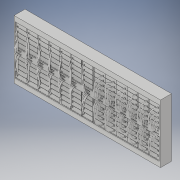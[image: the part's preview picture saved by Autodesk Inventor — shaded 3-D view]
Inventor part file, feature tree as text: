
AUTODESK INVENTOR PART (.ipt)
format: ipt  version: 2017 (Build 210142000, 142)  size: 6,932,992 bytes
history: native  units: in
note: dims shown in document units (in); Inventor stores cm internally (conversion verified against a paired STEP export)
features: sweep x35, sketch x5, extrude x3, mirror x2, plane x2, other x1
ambient origin geometry x8: Origin, YZ Plane, XZ Plane, XY Plane, X Axis, Y Axis, Z Axis, Center Point
bodies: Solid1 (feature_tree)
feature tree (48):
  extrude  "shelfing for towers"  Depth=20.0in
  other  "front of towers workplane"
  extrude  "front of towers"  Depth=0.0833in
  extrude  "towers defined"  Depth=0.5833in
  sketch  "Sketch4"  dims[d7=1.5in d8=2.9167in d9=1.5in d10=0.5833in d11=0.5833in d12=0.0833in d13=0.0833in d35=0.0833in d36=1.5in d37=2.9167in d38=1.5in d39=0.0in d40=-0.1in d47=1.5in d48=0.0in d60=0.5833in d61=0.01in d62=0.5833in d63=0.01in d64=0.5833in d65=0.01in d66=0.5833in d67=0.01in d68=0.01in d69=0.01in d70=0.01in d71=0.01in d72=0.005in d73=0.005in d74=0.005in d75=0.005in d79=0.005in d80=0.005in d81=0.005in d82=0.005in d83=0.005in d84=0.005in d85=0.005in d86=0.005in d88=0.01in d89=0.0in d90=1.5in d91=0.005in d92=0.01in d93=1.5in d94=0.01in d95=1.5in d96=0.01in d97=0.01in d98=1.5in d99=0.01in d100=1.5in d101=0.01in d102=0.01in d103=0.01in d104=0.01in d105=0.01in d106=0.01in d107=0.01in d108=0.01in d109=0.01in d110=0.01in d111=0.005in d112=0.2289in d115=0.125in d116=0.15in d117=0.15in d118=0.15in d119=0.15in d120=0.15in d121=0.125in d122=0.15in d123=0.15in d124=0.15in d125=0.15in d126=1.5in d127=0.125in d128=0.15in d129=0.15in d130=0.15in d131=0.15in d132=1.5in d133=0.125in d134=0.15in d135=0.15in d136=0.15in d137=0.15in d138=1.5in d139=0.125in d140=0.15in d141=0.15in d142=0.15in d143=0.15in d144=1.5in d145=0.125in d146=0.15in d147=0.15in d148=0.15in d149=0.15in d150=1.5in d187=0.125in d188=0.15in d189=0.15in d190=0.15in d191=0.15in d192=1.5in d193=0.2292in d194=0.15in d195=0.15in d196=0.15in d197=0.15in d198=0.15in d273=0.15in d274=0.15in d275=0.15in d276=0.15in d277=0.15in d286=1.5in d287=1.5in d288=1.5in d289=1.5in d290=1.5in d291=0.15in d293=0.15in d294=0.15in d295=0.15in d296=0.15in d297=0.15in d298=0.15in d300=0.15in d301=0.15in d302=0.15in d303=0.15in d304=0.15in d305=0.15in d306=0.15in d307=0.15in d308=0.15in d309=0.15in d310=0.15in d311=0.15in d312=0.15in d313=0.15in d314=0.15in d315=0.15in d316=90.0deg d317=90.0deg d318=0.25in d319=1.5in d320=1.5in d321=1.5in d322=1.5in d323=1.5in d330=1.5in d331=1.5in d332=1.5in d333=1.5in d334=1.5in d340=1.5in d344=1.5in d345=1.5in d346=1.5in d347=1.5in d348=1.5in d353=1.5in d354=1.5in d355=1.5in d356=1.5in d357=1.5in d362=1.5in d364=1.5in d366=1.5in d367=1.5in d368=1.5in d369=1.5in d370=1.5in d376=1.5in d377=1.5in d378=1.5in d379=1.5in d380=1.5in d386=1.5in d387=1.5in d388=1.5in d389=1.5in d390=1.5in d395=1.5in d396=1.5in d397=1.5in d398=1.5in d399=1.5in d404=1.5in d406=1.5in d408=1.5in d410=1.5in d411=0.5833in d527=0.125in d529=0.5833in d530=0.5833in d531=0.5833in d532=0.5833in d537=0.15in d538=0.3937in d539=0.3937in d540=0.3937in d541=0.3937in d542=0.3937in d543=0.3937in d544=0.3937in d545=0.3937in d546=0.3937in d547=0.3937in d548=0.0in d549=0.0in d550=0.0in d551=0.0in d552=0.0in d553=0.0in d554=0.0in d555=0.0in d556=0.3937in d557=0.3937in d558=0.0in d559=0.0in d560=0.0in d561=0.0in d562=0.3937in d563=0.3937in d564=0.3937in d565=0.3937in d566=0.3937in d567=0.3937in d568=0.3937in d569=0.3937in d570=0.0in d571=0.0in d572=0.0in d573=0.0in d574=0.0in d575=0.0in d576=0.0in d577=0.0in d578=0.3937in d579=0.3937in d580=0.3937in d581=0.3937in d582=0.3937in d583=0.3937in d584=0.3937in d585=0.3937in d586=0.3937in d587=0.3937in d588=0.0in d589=0.0in d590=0.0in d591=0.0in d592=0.0in d593=0.0in d594=0.0in d595=0.0in d596=0.0in d597=0.0in d598=0.06in d600=1.5in d601=0.3937in d602=0.3937in d603=0.3937in d604=0.3937in d605=0.3937in d606=0.3937in d607=0.3937in d608=0.3937in d609=0.3937in d610=0.3937in d611=0.3937in d612=0.3937in d613=0.3937in d614=0.3937in d615=0.3937in d616=0.3937in d617=0.3937in d618=0.3937in d619=0.3937in d620=0.3937in d621=0.06in d622=0.3937in d623=0.3937in d624=0.3937in d625=0.3937in d626=0.3937in d627=0.3937in d628=0.3937in d629=0.3937in d630=0.3937in d631=0.3937in d632=0.0in d633=0.0in d634=0.0in d635=0.0in d636=0.0in d637=0.0in d638=0.0in d639=0.0in d640=0.0in d641=0.0in d642=0.0in d643=0.0in d644=0.0in d645=0.0in d646=0.0in d647=0.0in d648=0.0in d649=0.0in d650=0.0in d651=0.0in d652=0.0in d653=0.0in d654=0.0in d655=0.0in d656=0.0in d657=0.0in d658=0.0in d659=0.0in d660=0.0in d661=0.0in d662=0.125in d663=0.25in d664=0.5833in d665=0.5833in d666=0.5833in d667=0.5833in d668=0.3937in d669=0.3937in d670=0.3937in d671=0.3937in d672=0.3937in d673=0.3937in d674=0.3937in d675=0.3937in d676=0.3937in d677=0.3937in d678=0.0in d679=0.0in d680=0.0in d681=0.0in d682=0.0in d683=0.0in d684=0.0in d685=0.0in d686=0.0in d687=0.0in]
  sketch  "3D Sketch1"
  sweep  "cable 1"
  sweep  "cable 2"
  sweep  "cable 3"
  sweep  "cable 4"
  sweep  "cable 5"
  sweep  "cable 6"
  sweep  "cable 7"
  sweep  "cable 8"
  sweep  "cable 9"
  sweep  "cable 10"
  sweep  "cable 11"
  sweep  "cable 12"
  sweep  "cable 13"
  sweep  "cable 14"
  sweep  "cable 15"
  sweep  "cable 16"
  sweep  "cable 17"
  sweep  "cable 18"
  sweep  "cable 19"
  sweep  "cable 20"
  sweep  "cable 21"
  sweep  "cable 22"
  sweep  "cable 23"
  sweep  "cable 24"
  sweep  "cable 25"
  sweep  "cable 26"
  sweep  "cable 27"
  sweep  "cable 28"
  sweep  "cable 29"
  sweep  "cable 30"
  sweep  "cable 31"
  sweep  "cable 32"
  sweep  "cable 33"
  sweep  "cable 34"
  sweep  "cable 35"
  mirror  "Mirror1"
  mirror  "Mirror2"
  sketch  "Sketch1"  dims[d0=8.0in d1=20.0in]
  sketch  "Sketch2"  dims[d2=0.0833in d4=0.0833in]
  sketch  "Sketch3"  dims[d5=0.0833in d6=0.5833in]
  plane  "Work Plane2"
  plane  "Work Plane3"
